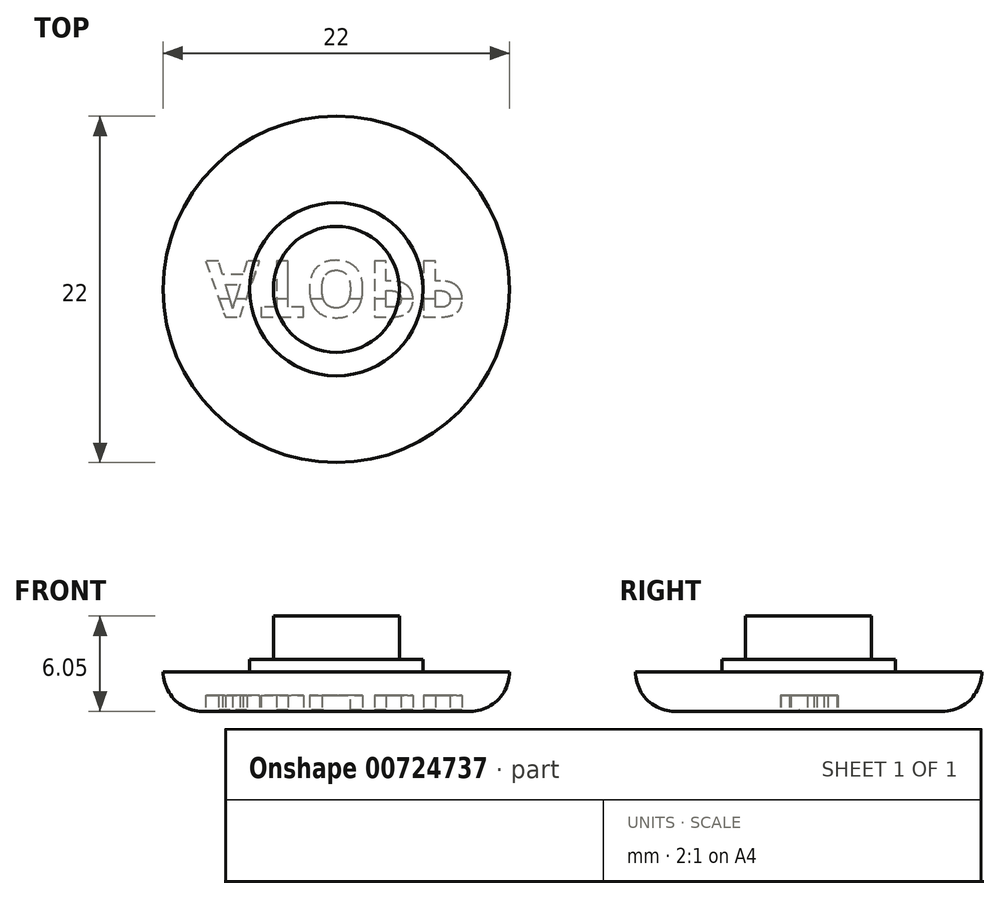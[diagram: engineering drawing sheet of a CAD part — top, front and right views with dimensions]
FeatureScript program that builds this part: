
annotation { "Feature Type Name" : "Feature", "Feature Type Description" : "" }
export const myFeature = defineFeature(function(context is Context, id is Id, definition is map)
    precondition{}
    {
        {
            var Q0;
            Q0=qCreatedBy(makeId("Top.planeOp"),FACE);
            var sketch = newSketch(context, id + "F0", { "sketchPlane" : qUnion([Q0])});
            skCircle(sketch, "E0", {"center": v(0, 0) * mm, "radius": 11 * mm});
            skCircle(sketch, "E1", {"center": v(0, 0) * mm, "radius": 4 * mm});
            skCircle(sketch, "E2", {"center": v(0, 0) * mm, "radius": 5.5 * mm});
            skSolve(sketch);
        }
        {
            var Q0;
            Q0=makeQuery(id+"F0.imprint","IMPRINT",FACE,{"disambiguationData":[TD([[makeQuery(id+"F0.imprint","IMPRINT",EDGE,{"derivedFrom":sQuery(id+"F0.wireOp",EDGE,"E0")}),1.0]])]});
            extrude(context, id + "F1", {"entities" : qUnion([Q0]), "depth" : 2.5 * mm, "offsetDistance" : 25 * mm});
        }
        {
            var Q0;
            Q0=makeQuery(id+"F0.imprint","IMPRINT",FACE,{"disambiguationData":[TD([[makeQuery(id+"F0.imprint","IMPRINT",EDGE,{"derivedFrom":sQuery(id+"F0.wireOp",EDGE,"E1")}),-1.0]])]});
            var Q1;
            Q1=makeQuery(id+"F1.opExtrude","CAP_FACE",FACE,{"disambiguationData":[OSD([sQuery(id+"F0.wireOp",EDGE,"E0"),sQuery(id+"F0.wireOp",EDGE,"E2")])],"isStart":false});
            extrude(context, id + "F2", {"entities" : qUnion([Q0]), "operationType" : NewBodyOperationType.ADD, "endBound" : BoundingType.UP_TO_SURFACE, "depth" : 25 * mm, "endBoundEntityFace" : qUnion([Q1]), "hasOffset" : true, "offsetDistance" : .8 * mm, "offsetOppositeDirection" : true});
        }
        {
            var Q0;
            Q0=makeQuery(id+"F0.imprint","IMPRINT",FACE,{"disambiguationData":[TD([[makeQuery(id+"F0.imprint","IMPRINT",EDGE,{"derivedFrom":sQuery(id+"F0.wireOp",EDGE,"E1")}),1.0]])]});
            var Q1;
            Q1=makeQuery(id+"F2.opExtrude","CAP_FACE",FACE,{"disambiguationData":[OSD([sQuery(id+"F0.wireOp",EDGE,"E0"),sQuery(id+"F0.wireOp",EDGE,"E2")])],"isStart":false});
            extrude(context, id + "F3", {"entities" : qUnion([Q0]), "operationType" : NewBodyOperationType.ADD, "endBound" : BoundingType.UP_TO_SURFACE, "depth" : 3 * mm, "endBoundEntityFace" : qUnion([Q1]), "hasOffset" : true, "offsetDistance" : 2.75 * mm, "offsetOppositeDirection" : true});
        }
        {
            var Q0;
            {var subQ0=sQuery(id+"F0.wireOp",EDGE,"E1");var subQ1=sQuery(id+"F0.wireOp",EDGE,"E2");Q0=makeQuery(id+"F3.boolean.opBoolean","MERGE",FACE,{"derivedFrom":[makeQuery(id+"F2.boolean.opBoolean","MERGE",FACE,{"derivedFrom":[makeQuery(id+"F1.opExtrude","CAP_FACE",FACE,{"disambiguationData":[OSD([sQuery(id+"F0.wireOp",EDGE,"E0"),subQ1])],"isStart":true}),makeQuery(id+"F2.opExtrude","CAP_FACE",FACE,{"disambiguationData":[OSD([subQ0,subQ1])],"isStart":true})]}),makeQuery(id+"F3.opExtrude","CAP_FACE",FACE,{"disambiguationData":[OSD([subQ0])],"isStart":true})]});}
            fillet(context, id + "F4", {"entities" : qUnion([Q0]), "radius" : 2.5 * mm, "tangentPropagation" : true, "allowEdgeOverflow" : false});
        }
        {
            var Q0;
            Q0=qCreatedBy(makeId("Right.planeOp"),FACE);
            var sketch = newSketch(context, id + "F5", { "sketchPlane" : qUnion([Q0])});
            skEllipse(sketch, "E3", {"center": v(-63.43, -1.89) * mm, "majorRadius": 11 * mm, "minorRadius": 2.5 * mm, "majorAxis": v(-1, 0)});
            skPoint(sketch, "E4", {"position": v(-63.43, 0.61) * mm});
            skLineSegment(sketch, "E5", {"start": v(-55.79, 0) * mm, "end": v(-71.08, 0) * mm});
            skArc(sketch, "E6", {"start": v(-11, 2.37) * mm, "mid": v(-6, 2.57) * mm, "end": v(-11, 2.5) * mm});
            skArc(sketch, "E7", {"start": v(6, 2.5) * mm, "mid": v(6, 2.46) * mm, "end": v(6, 2.42) * mm});
            skLineSegment(sketch, "E8", {"start": v(-63.43, 0.61) * mm, "end": v(-63.43, -4.39) * mm});
            skPoint(sketch, "E9.orphan", {"position": v(-63.43, -3.78) * mm});
            skPoint(sketch, "E10.orphan", {"position": v(-63.43, 0) * mm});
            skSolve(sketch);
        }
        {
            var Q0;
            {var subQ0=sQuery(id+"F0.wireOp",EDGE,"E1");var subQ1=sQuery(id+"F0.wireOp",EDGE,"E2");Q0=makeQuery(id+"F3.boolean.opBoolean","MERGE",FACE,{"derivedFrom":[makeQuery(id+"F2.boolean.opBoolean","MERGE",FACE,{"derivedFrom":[makeQuery(id+"F1.opExtrude","CAP_FACE",FACE,{"disambiguationData":[OSD([sQuery(id+"F0.wireOp",EDGE,"E0"),subQ1])],"isStart":true}),makeQuery(id+"F2.opExtrude","CAP_FACE",FACE,{"disambiguationData":[OSD([subQ0,subQ1])],"isStart":true})]}),makeQuery(id+"F3.opExtrude","CAP_FACE",FACE,{"disambiguationData":[OSD([subQ0])],"isStart":true})]});}
            var sketch = newSketch(context, id + "F6", { "sketchPlane" : qUnion([Q0])});
            skSolve(sketch);
        }
        {
            var Q0;
            {var subQ0=sQuery(id+"F0.wireOp",EDGE,"E1");var subQ1=sQuery(id+"F0.wireOp",EDGE,"E2");var subQ2=sQuery(id+"F0.wireOp",EDGE,"E0");Q0=makeQuery(id+"F6.imprint","IMPRINT",FACE,{"disambiguationData":[TD([[makeQuery(id+"F6.imprint","IMPRINT",EDGE,{"derivedFrom":makeQuery(id+"F4.opFillet","BLEND_EDGE",EDGE,{"blendedFrom":[makeQuery(id+"F1.opExtrude","CAP_EDGE",EDGE,{"disambiguationData":[OSD([subQ2])],"isStart":true}),makeQuery(id+"F3.boolean.opBoolean","MERGE",FACE,{"derivedFrom":[makeQuery(id+"F2.boolean.opBoolean","MERGE",FACE,{"derivedFrom":[makeQuery(id+"F1.opExtrude","CAP_FACE",FACE,{"disambiguationData":[OSD([subQ2,subQ1])],"isStart":true}),makeQuery(id+"F2.opExtrude","CAP_FACE",FACE,{"disambiguationData":[OSD([subQ0,subQ1])],"isStart":true})]}),makeQuery(id+"F3.opExtrude","CAP_FACE",FACE,{"disambiguationData":[OSD([subQ0])],"isStart":true})]})],"blendedInto":[makeQuery(id+"F3.boolean.opBoolean","MERGE",FACE,{"derivedFrom":[makeQuery(id+"F2.boolean.opBoolean","MERGE",FACE,{"derivedFrom":[makeQuery(id+"F1.opExtrude","CAP_FACE",FACE,{"disambiguationData":[OSD([subQ2,subQ1])],"isStart":true}),makeQuery(id+"F2.opExtrude","CAP_FACE",FACE,{"disambiguationData":[OSD([subQ0,subQ1])],"isStart":true})]}),makeQuery(id+"F3.opExtrude","CAP_FACE",FACE,{"disambiguationData":[OSD([subQ0])],"isStart":true})]})]})}),1.0]])]});}
            var sketch = newSketch(context, id + "F7", { "sketchPlane" : qUnion([Q0])});
            skLineSegment(sketch, "E11", {"start": v(-8.5, 0) * mm, "end": v(8.5, 0) * mm});
            skText(sketch, "E12", { "text": "ATOPP", "fontName": "OpenSans-Bold.ttf"});
            const initialGuessF7  = {"E12": [-0.0083, -0.0018, 1, 0, 0.00358]};
            skSetInitialGuess(sketch, initialGuessF7);
            skSolve(sketch);
        }
        {
            var Q0;
            Q0=qSketchRegion(id+"F7",true);
            extrude(context, id + "F8", {"entities" : qUnion([Q0]), "operationType" : NewBodyOperationType.REMOVE, "oppositeDirection" : true, "depth" : 1 * mm, "offsetDistance" : 25 * mm});
        }
        {
            var Q0;
            {var subQ0=sQuery(id+"F0.wireOp",EDGE,"E1");var subQ1=sQuery(id+"F0.wireOp",EDGE,"E2");var subQ2=sQuery(id+"F0.wireOp",EDGE,"E0");Q0=makeQuery(id+"F6.imprint","IMPRINT",FACE,{"disambiguationData":[TD([[makeQuery(id+"F6.imprint","IMPRINT",EDGE,{"derivedFrom":makeQuery(id+"F4.opFillet","BLEND_EDGE",EDGE,{"blendedFrom":[makeQuery(id+"F1.opExtrude","CAP_EDGE",EDGE,{"disambiguationData":[OSD([subQ2])],"isStart":true}),makeQuery(id+"F3.boolean.opBoolean","MERGE",FACE,{"derivedFrom":[makeQuery(id+"F2.boolean.opBoolean","MERGE",FACE,{"derivedFrom":[makeQuery(id+"F1.opExtrude","CAP_FACE",FACE,{"disambiguationData":[OSD([subQ2,subQ1])],"isStart":true}),makeQuery(id+"F2.opExtrude","CAP_FACE",FACE,{"disambiguationData":[OSD([subQ0,subQ1])],"isStart":true})]}),makeQuery(id+"F3.opExtrude","CAP_FACE",FACE,{"disambiguationData":[OSD([subQ0])],"isStart":true})]})],"blendedInto":[makeQuery(id+"F3.boolean.opBoolean","MERGE",FACE,{"derivedFrom":[makeQuery(id+"F2.boolean.opBoolean","MERGE",FACE,{"derivedFrom":[makeQuery(id+"F1.opExtrude","CAP_FACE",FACE,{"disambiguationData":[OSD([subQ2,subQ1])],"isStart":true}),makeQuery(id+"F2.opExtrude","CAP_FACE",FACE,{"disambiguationData":[OSD([subQ0,subQ1])],"isStart":true})]}),makeQuery(id+"F3.opExtrude","CAP_FACE",FACE,{"disambiguationData":[OSD([subQ0])],"isStart":true})]})]})}),1.0]])]});}
            var sketch = newSketch(context, id + "F9", { "sketchPlane" : qUnion([Q0])});
            skLineSegment(sketch, "E13.bottom", {"start": v(8.21, 0.6) * mm, "end": v(-8.21, 0.6) * mm});
            skLineSegment(sketch, "E13.top", {"start": v(8.21, 0.6) * mm, "end": v(-8.21, 0.6) * mm});
            skLineSegment(sketch, "E13.left", {"start": v(8.21, 0.6) * mm, "end": v(8.21, 0.6) * mm});
            skLineSegment(sketch, "E13.right", {"start": v(-8.21, 0.6) * mm, "end": v(-8.21, 0.6) * mm});
            skPoint(sketch, "E13.middle", {"position": v(0, 0.6) * mm});
            skSolve(sketch);
        }
        {
            var Q0;
            Q0 = qSketchRegion(id + "F9", true);
            extrude(context, id + "F10", {"entities" : qUnion([Q0]), "operationType" : NewBodyOperationType.ADD, "oppositeDirection" : true, "depth" : .1 * mm, "offsetDistance" : 25 * mm});
        }
    });
